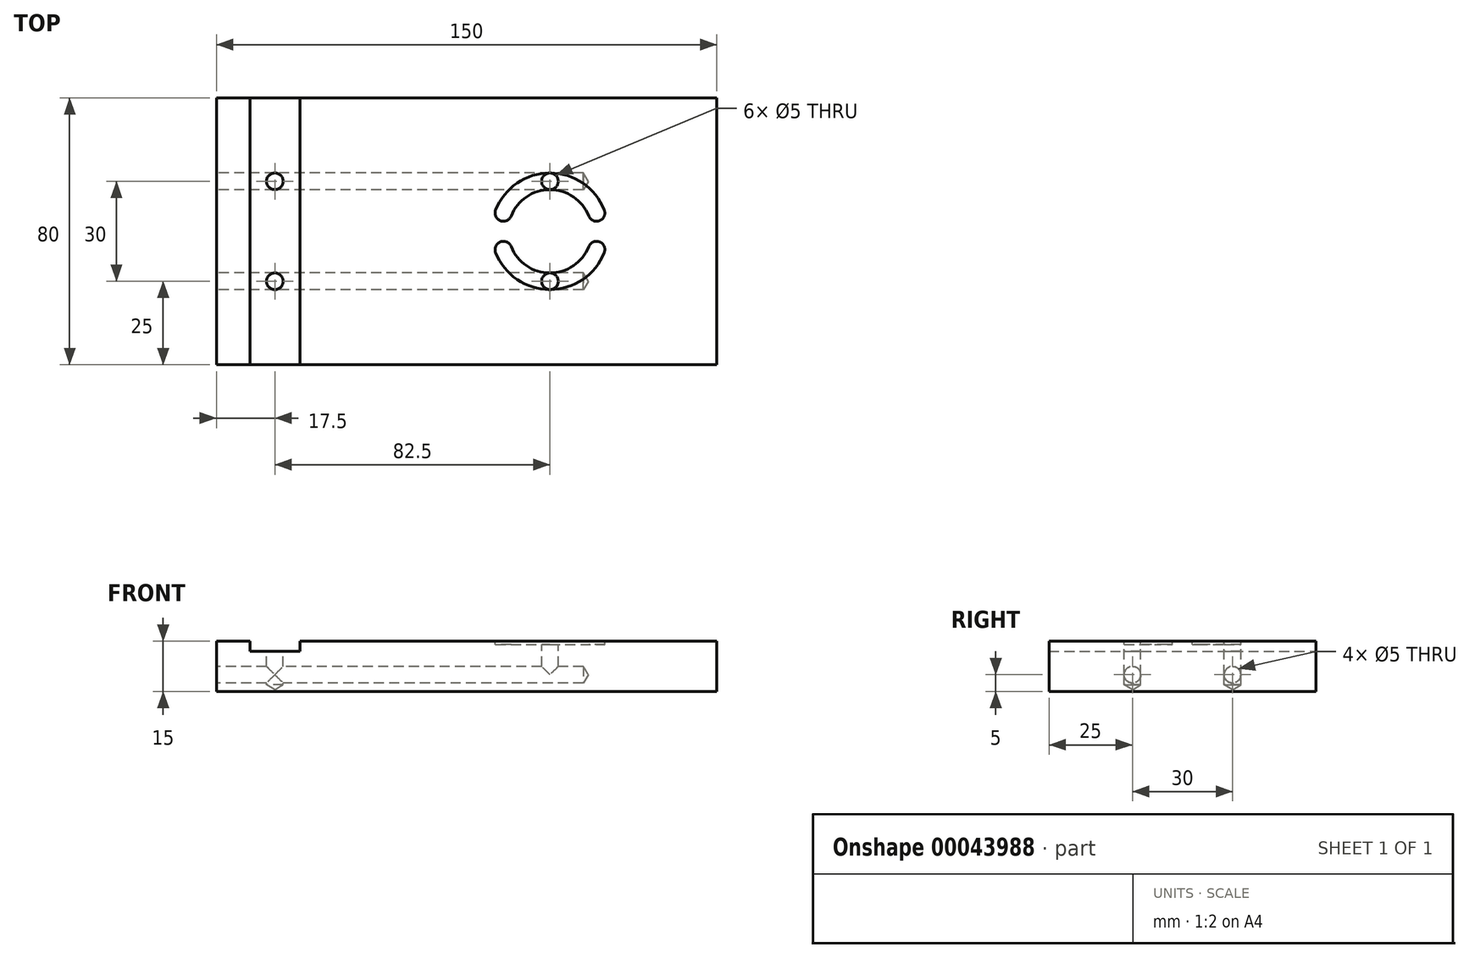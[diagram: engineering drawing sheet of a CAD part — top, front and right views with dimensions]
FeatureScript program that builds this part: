
annotation { "Feature Type Name" : "Feature", "Feature Type Description" : "" }
export const myFeature = defineFeature(function(context is Context, id is Id, definition is map)
    precondition{}
    {
        {
            var Q0;
            Q0=qCreatedBy(makeId("Top.planeOp"),FACE);
            var sketch = newSketch(context, id + "F0", { "sketchPlane" : qUnion([Q0])});
            skLineSegment(sketch, "E0.rect.bottom", {"start": v(75, 40) * mm, "end": v(-75, 40) * mm});
            skLineSegment(sketch, "E0.rect.top", {"start": v(75, -40) * mm, "end": v(-75, -40) * mm});
            skLineSegment(sketch, "E0.rect.left", {"start": v(75, 40) * mm, "end": v(75, -40) * mm});
            skLineSegment(sketch, "E0.rect.right", {"start": v(-75, 40) * mm, "end": v(-75, -40) * mm});
            skPoint(sketch, "E0.rect.middle", {"position": v(0, 0) * mm});
            skSolve(sketch);
        }
        {
            var Q0;
            Q0 = qSketchRegion(id + "F0", true);
            extrude(context, id + "F1", {"entities" : qUnion([Q0]), "depth" : 15 * mm});
        }
        {
            var Q0;
            Q0=makeQuery(id+"F1.opExtrude","CAP_FACE",FACE,{"disambiguationData":[OSD([sQuery(id+"F0.wireOp",EDGE,"E0.rect.bottom"),sQuery(id+"F0.wireOp",EDGE,"E0.rect.top"),sQuery(id+"F0.wireOp",EDGE,"E0.rect.left"),sQuery(id+"F0.wireOp",EDGE,"E0.rect.right")])],"isStart":false});
            var sketch = newSketch(context, id + "F12", { "sketchPlane" : qUnion([Q0])});
            skLineSegment(sketch, "E1.bottom", {"start": v(-65, -40) * mm, "end": v(-50, -40) * mm});
            skLineSegment(sketch, "E1.top", {"start": v(-65, 40) * mm, "end": v(-50, 40) * mm});
            skLineSegment(sketch, "E1.left", {"start": v(-65, -40) * mm, "end": v(-65, 40) * mm});
            skLineSegment(sketch, "E1.right", {"start": v(-50, -40) * mm, "end": v(-50, 40) * mm});
            skSolve(sketch);
        }
        {
            var Q0;
            Q0 = qSketchRegion(id + "F12", true);
            var sketch = newSketch(context, id + "F2", { "sketchPlane" : qUnion([Q0])});
            skSolve(sketch);
        }
        {
            var Q0;
            Q0=makeQuery(id+"F12.imprint","IMPRINT",FACE,{"disambiguationData":[TD([[makeQuery(id+"F12.imprint","IMPRINT",EDGE,{"derivedFrom":sQuery(id+"F12.wireOp",EDGE,"E1.bottom")}),-1.0]])]});
            var Q1;
            Q1 = qSketchRegion(id + "F12", true);
            extrude(context, id + "F13", {"entities" : qUnion([Q0, Q1]), "operationType" : NewBodyOperationType.REMOVE, "oppositeDirection" : true, "depth" : 3 * mm});
        }
        {
            var Q0;
            Q0=makeQuery(id+"F1.opExtrude","SWEPT_FACE",FACE,{"disambiguationData":[OSD([sQuery(id+"F0.wireOp",EDGE,"E0.rect.right")])]});
            var sketch = newSketch(context, id + "F3", { "sketchPlane" : qUnion([Q0])});
            skPoint(sketch, "E2", {"position": v(-15, 5) * mm});
            skPoint(sketch, "E3", {"position": v(15, 5) * mm});
            skSolve(sketch);
        }
        {
            var Q0;
            Q0=sQuery(id+"F3.wireOp",VERTEX,"E2");
            var Q1;
            Q1=sQuery(id+"F3.wireOp",VERTEX,"E3");
            var Q2;
            Q2=makeQuery(id+"F1.opExtrude","SWEPT_BODY",BODY,{"disambiguationData":[OSD([sQuery(id+"F0.wireOp",EDGE,"E0.rect.bottom"),sQuery(id+"F0.wireOp",EDGE,"E0.rect.top"),sQuery(id+"F0.wireOp",EDGE,"E0.rect.left"),sQuery(id+"F0.wireOp",EDGE,"E0.rect.right")])]});
            hole(context, id + "F4", {"style" : HoleStyle.SIMPLE, "holeDiameter" : 5 * mm, "endStyle" : HoleEndStyle.BLIND, "holeDepth" : 110 * mm, "locations" : qUnion([Q0, Q1]), "scope" : qUnion([Q2])});
        }
        {
            var Q0;
            {var subQ0=sQuery(id+"F0.wireOp",EDGE,"E0.rect.bottom");var subQ1=sQuery(id+"F0.wireOp",EDGE,"E0.rect.top");var subQ2=sQuery(id+"F0.wireOp",EDGE,"E0.rect.left");Q0=makeQuery(id+"F13.boolean.opBoolean","SPLIT",FACE,{"disambiguationData":[TD([makeQuery(id+"F1.opExtrude","SWEPT_FACE",FACE,{"disambiguationData":[OSD([subQ2])]})])],"derivedFrom":makeQuery(id+"F1.opExtrude","CAP_FACE",FACE,{"disambiguationData":[OSD([subQ0,subQ1,subQ2,sQuery(id+"F0.wireOp",EDGE,"E0.rect.right")])],"isStart":false})});}
            var sketch = newSketch(context, id + "F5", { "sketchPlane" : qUnion([Q0])});
            skLineSegment(sketch, "E4.0", {"start": v(-75, 12.5) * mm, "end": v(-75, 17.5) * mm});
            skLineSegment(sketch, "E5", {"start": v(-75, 17.5) * mm, "end": v(35, 17.5) * mm});
            skLineSegment(sketch, "E6", {"start": v(35, 12.5) * mm, "end": v(-75, 12.5) * mm});
            skLineSegment(sketch, "E7", {"start": v(-75, -12.5) * mm, "end": v(35, -12.5) * mm});
            skLineSegment(sketch, "E8", {"start": v(35, -17.5) * mm, "end": v(-75, -17.5) * mm});
            skPoint(sketch, "E9", {"position": v(25, 15) * mm});
            skPoint(sketch, "E10", {"position": v(25, -15) * mm});
            skSolve(sketch);
        }
        {
            var Q0;
            Q0=sQuery(id+"F5.wireOp",VERTEX,"E9");
            var Q1;
            Q1=sQuery(id+"F5.wireOp",VERTEX,"E10");
            var Q2;
            Q2=makeQuery(id+"F1.opExtrude","SWEPT_BODY",BODY,{"disambiguationData":[OSD([sQuery(id+"F0.wireOp",EDGE,"E0.rect.bottom"),sQuery(id+"F0.wireOp",EDGE,"E0.rect.top"),sQuery(id+"F0.wireOp",EDGE,"E0.rect.left"),sQuery(id+"F0.wireOp",EDGE,"E0.rect.right")])]});
            hole(context, id + "F6", {"style" : HoleStyle.SIMPLE, "holeDiameter" : 5 * mm, "endStyle" : HoleEndStyle.BLIND, "holeDepth" : 10 * mm, "locations" : qUnion([Q0, Q1]), "scope" : qUnion([Q2])});
        }
        {
            var Q0;
            {var subQ0=sQuery(id+"F0.wireOp",EDGE,"E0.rect.bottom");var subQ1=sQuery(id+"F0.wireOp",EDGE,"E0.rect.top");var subQ2=sQuery(id+"F0.wireOp",EDGE,"E0.rect.left");Q0=makeQuery(id+"F13.boolean.opBoolean","SPLIT",FACE,{"disambiguationData":[TD([makeQuery(id+"F1.opExtrude","SWEPT_FACE",FACE,{"disambiguationData":[OSD([subQ2])]})])],"derivedFrom":makeQuery(id+"F1.opExtrude","CAP_FACE",FACE,{"disambiguationData":[OSD([subQ0,subQ1,subQ2,sQuery(id+"F0.wireOp",EDGE,"E0.rect.right")])],"isStart":false})});}
            var sketch = newSketch(context, id + "F7", { "sketchPlane" : qUnion([Q0])});
            skLineSegment(sketch, "E11", {"start": v(25, 15) * mm, "end": v(25, -15) * mm});
            skArc(sketch, "E12", {"start": v(13.37, -4.58) * mm, "mid": v(25, -12.5) * mm, "end": v(36.63, -4.58) * mm});
            skArc(sketch, "E13", {"start": v(8.72, -6.42) * mm, "mid": v(25, -17.5) * mm, "end": v(41.28, -6.42) * mm});
            skLineSegment(sketch, "E14", {"start": v(11.04, 3) * mm, "end": v(11.04, 3) * mm});
            skLineSegment(sketch, "E15", {"start": v(11.04, -3) * mm, "end": v(11.04, -3) * mm});
            skPoint(sketch, "E16.orphan", {"position": v(0, -3) * mm});
            skLineSegment(sketch, "E17.trimOffspring", {"start": v(38.96, -3) * mm, "end": v(38.96, -3) * mm});
            skLineSegment(sketch, "E18.trimOffspring", {"start": v(38.96, 3) * mm, "end": v(38.96, 3) * mm});
            skArc(sketch, "E19.trimOffspring", {"start": v(41.28, 6.42) * mm, "mid": v(25, 17.5) * mm, "end": v(8.72, 6.42) * mm});
            skArc(sketch, "E20.trimOffspring", {"start": v(36.63, 4.58) * mm, "mid": v(25, 12.5) * mm, "end": v(13.37, 4.58) * mm});
            skPoint(sketch, "E21.visualSharp", {"position": v(12.87, 3) * mm});
            skArc(sketch, "E21.filletArc", {"start": v(11.04, 3) * mm, "mid": v(12.45, 3.43) * mm, "end": v(13.37, 4.58) * mm});
            skPoint(sketch, "E22.visualSharp", {"position": v(37.13, 3) * mm});
            skArc(sketch, "E22.filletArc", {"start": v(36.63, 4.58) * mm, "mid": v(37.55, 3.43) * mm, "end": v(38.96, 3) * mm});
            skPoint(sketch, "E23.visualSharp", {"position": v(42.24, -3) * mm});
            skArc(sketch, "E23.filletArc", {"start": v(41.28, -6.42) * mm, "mid": v(41.02, -4.1) * mm, "end": v(38.96, -3) * mm});
            skPoint(sketch, "E24.visualSharp", {"position": v(37.13, -3) * mm});
            skArc(sketch, "E24.filletArc", {"start": v(38.96, -3) * mm, "mid": v(37.55, -3.43) * mm, "end": v(36.63, -4.58) * mm});
            skPoint(sketch, "E25.visualSharp", {"position": v(7.76, -3) * mm});
            skArc(sketch, "E25.filletArc", {"start": v(11.04, -3) * mm, "mid": v(8.98, -4.1) * mm, "end": v(8.72, -6.42) * mm});
            skPoint(sketch, "E26.visualSharp", {"position": v(12.87, -3) * mm});
            skArc(sketch, "E26.filletArc", {"start": v(13.37, -4.58) * mm, "mid": v(12.45, -3.43) * mm, "end": v(11.04, -3) * mm});
            skPoint(sketch, "E27.visualSharp", {"position": v(42.24, 3) * mm});
            skArc(sketch, "E27.filletArc", {"start": v(38.96, 3) * mm, "mid": v(41.02, 4.1) * mm, "end": v(41.28, 6.42) * mm});
            skPoint(sketch, "E28.visualSharp", {"position": v(7.76, 3) * mm});
            skArc(sketch, "E28.filletArc", {"start": v(8.72, 6.42) * mm, "mid": v(8.98, 4.1) * mm, "end": v(11.04, 3) * mm});
            skSolve(sketch);
        }
        {
            var Q0;
            Q0 = qSketchRegion(id + "F7", true);
            extrude(context, id + "F8", {"entities" : qUnion([Q0]), "operationType" : NewBodyOperationType.REMOVE, "oppositeDirection" : true, "depth" : 1 * mm});
        }
        {
            var Q0;
            Q0=makeQuery(id+"F2.imprint","IMPRINT",FACE,{"disambiguationData":[TD([[makeQuery(id+"F2.imprint","IMPRINT",EDGE,{"derivedFrom":makeQuery(id+"F12.imprint","IMPRINT",EDGE,{"derivedFrom":sQuery(id+"F12.wireOp",EDGE,"E1.bottom")})}),-1.0]])]});
            var sketch = newSketch(context, id + "F9", { "sketchPlane" : qUnion([Q0])});
            skArc(sketch, "E29.0", {"start": v(25, 17.5) * mm, "mid": v(22.5, 15) * mm, "end": v(25, 12.5) * mm});
            skArc(sketch, "E30.0", {"start": v(25, -12.5) * mm, "mid": v(22.5, -15) * mm, "end": v(25, -17.5) * mm});
            skLineSegment(sketch, "E31.0", {"start": v(-50, 40) * mm, "end": v(-65, 40) * mm});
            skPoint(sketch, "E32", {"position": v(-57.5, -15) * mm});
            skPoint(sketch, "E33", {"position": v(-57.5, 15) * mm});
            skSolve(sketch);
        }
        {
            var Q0;
            Q0=sQuery(id+"F9.wireOp",VERTEX,"E33");
            var Q1;
            Q1=sQuery(id+"F9.wireOp",VERTEX,"E32");
            var Q2;
            Q2=makeQuery(id+"F1.opExtrude","SWEPT_BODY",BODY,{"disambiguationData":[OSD([sQuery(id+"F0.wireOp",EDGE,"E0.rect.bottom"),sQuery(id+"F0.wireOp",EDGE,"E0.rect.top"),sQuery(id+"F0.wireOp",EDGE,"E0.rect.left"),sQuery(id+"F0.wireOp",EDGE,"E0.rect.right")])]});
            hole(context, id + "F10", {"style" : HoleStyle.SIMPLE, "holeDiameter" : 5 * mm, "endStyle" : HoleEndStyle.BLIND, "holeDepth" : 10 * mm, "locations" : qUnion([Q0, Q1]), "scope" : qUnion([Q2])});
        }
    });
